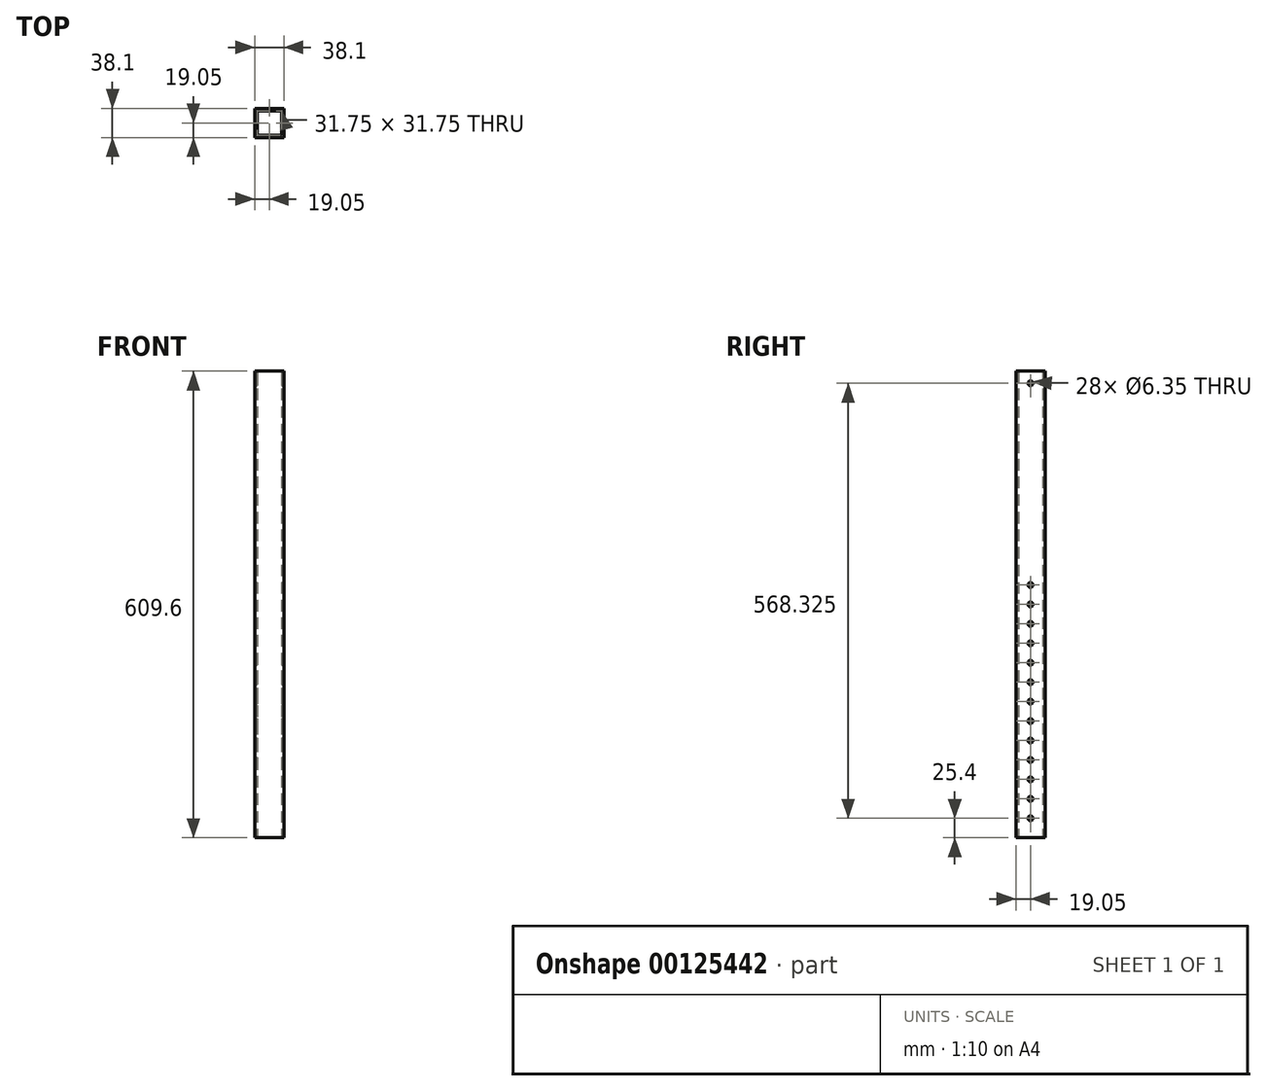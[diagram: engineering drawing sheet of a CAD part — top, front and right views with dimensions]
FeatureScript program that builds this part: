
annotation { "Feature Type Name" : "Feature", "Feature Type Description" : "" }
export const myFeature = defineFeature(function(context is Context, id is Id, definition is map)
    precondition{}
    {
        {
            var Q0;
            Q0=qCreatedBy(makeId("Top.planeOp"),FACE);
            var sketch = newSketch(context, id + "F0", { "sketchPlane" : qUnion([Q0])});
            skLineSegment(sketch, "E0.bottom", {"start": v(15.88, -15.87) * mm, "end": v(-15.88, -15.88) * mm});
            skLineSegment(sketch, "E0.top", {"start": v(15.88, 15.88) * mm, "end": v(-15.88, 15.87) * mm});
            skLineSegment(sketch, "E0.left", {"start": v(15.88, -15.88) * mm, "end": v(15.87, 15.88) * mm});
            skLineSegment(sketch, "E0.right", {"start": v(-15.88, -15.88) * mm, "end": v(-15.88, 15.88) * mm});
            skPoint(sketch, "E0.middle", {"position": v(0, 0) * mm});
            skLineSegment(sketch, "E1.bottom", {"start": v(19.05, -19.05) * mm, "end": v(-19.05, -19.05) * mm});
            skLineSegment(sketch, "E1.top", {"start": v(19.05, 19.05) * mm, "end": v(-19.05, 19.05) * mm});
            skLineSegment(sketch, "E1.left", {"start": v(19.05, -19.05) * mm, "end": v(19.05, 19.05) * mm});
            skLineSegment(sketch, "E1.right", {"start": v(-19.05, -19.05) * mm, "end": v(-19.05, 19.05) * mm});
            skSolve(sketch);
        }
        {
            var Q0;
            Q0=makeQuery(id+"F0.imprint","IMPRINT",FACE,{"disambiguationData":[TD([[makeQuery(id+"F0.imprint","IMPRINT",EDGE,{"derivedFrom":sQuery(id+"F0.wireOp",EDGE,"E0.bottom")}),1.0]])]});
            extrude(context, id + "F1", {"entities" : qUnion([Q0]), "endBound" : BoundingType.SYMMETRIC, "depth" : 609.6 * mm});
        }
        {
            var Q0;
            Q0=qCreatedBy(makeId("Right.planeOp"),FACE);
            var sketch = newSketch(context, id + "F2", { "sketchPlane" : qUnion([Q0])});
            skCircle(sketch, "E2", {"center": v(0, -177.8) * mm, "radius": 3.18 * mm});
            skCircle(sketch, "E3", {"center": v(0, -203.2) * mm, "radius": 3.18 * mm});
            skCircle(sketch, "E4", {"center": v(0, -228.6) * mm, "radius": 3.18 * mm});
            skCircle(sketch, "E5", {"center": v(0, -254) * mm, "radius": 3.18 * mm});
            skCircle(sketch, "E6", {"center": v(0, -279.4) * mm, "radius": 3.18 * mm});
            skCircle(sketch, "E7", {"center": v(0, -152.4) * mm, "radius": 3.18 * mm});
            skCircle(sketch, "E8", {"center": v(0, -127) * mm, "radius": 3.18 * mm});
            skLineSegment(sketch, "E9", {"start": v(22.8, -127) * mm, "end": v(-22.15, -127) * mm});
            skCircle(sketch, "E10.MirrorC", {"center": v(0, -101.6) * mm, "radius": 3.18 * mm});
            skCircle(sketch, "E11.MirrorC", {"center": v(0, 25.4) * mm, "radius": 3.18 * mm});
            skCircle(sketch, "E12.MirrorC", {"center": v(0, -50.8) * mm, "radius": 3.18 * mm});
            skCircle(sketch, "E13.MirrorC", {"center": v(0, 0) * mm, "radius": 3.18 * mm});
            skCircle(sketch, "E14.MirrorC", {"center": v(0, -25.4) * mm, "radius": 3.18 * mm});
            skCircle(sketch, "E15.MirrorC", {"center": v(0, -76.2) * mm, "radius": 3.18 * mm});
            skCircle(sketch, "E16", {"center": v(0, 288.93) * mm, "radius": 3.18 * mm});
            skSolve(sketch);
        }
        {
            var Q0;
            Q0 = qSketchRegion(id + "F2", true);
            extrude(context, id + "F3", {"entities" : qUnion([Q0]), "operationType" : NewBodyOperationType.REMOVE, "endBound" : BoundingType.SYMMETRIC, "oppositeDirection" : true, "depth" : 44.45 * mm});
        }
    });
